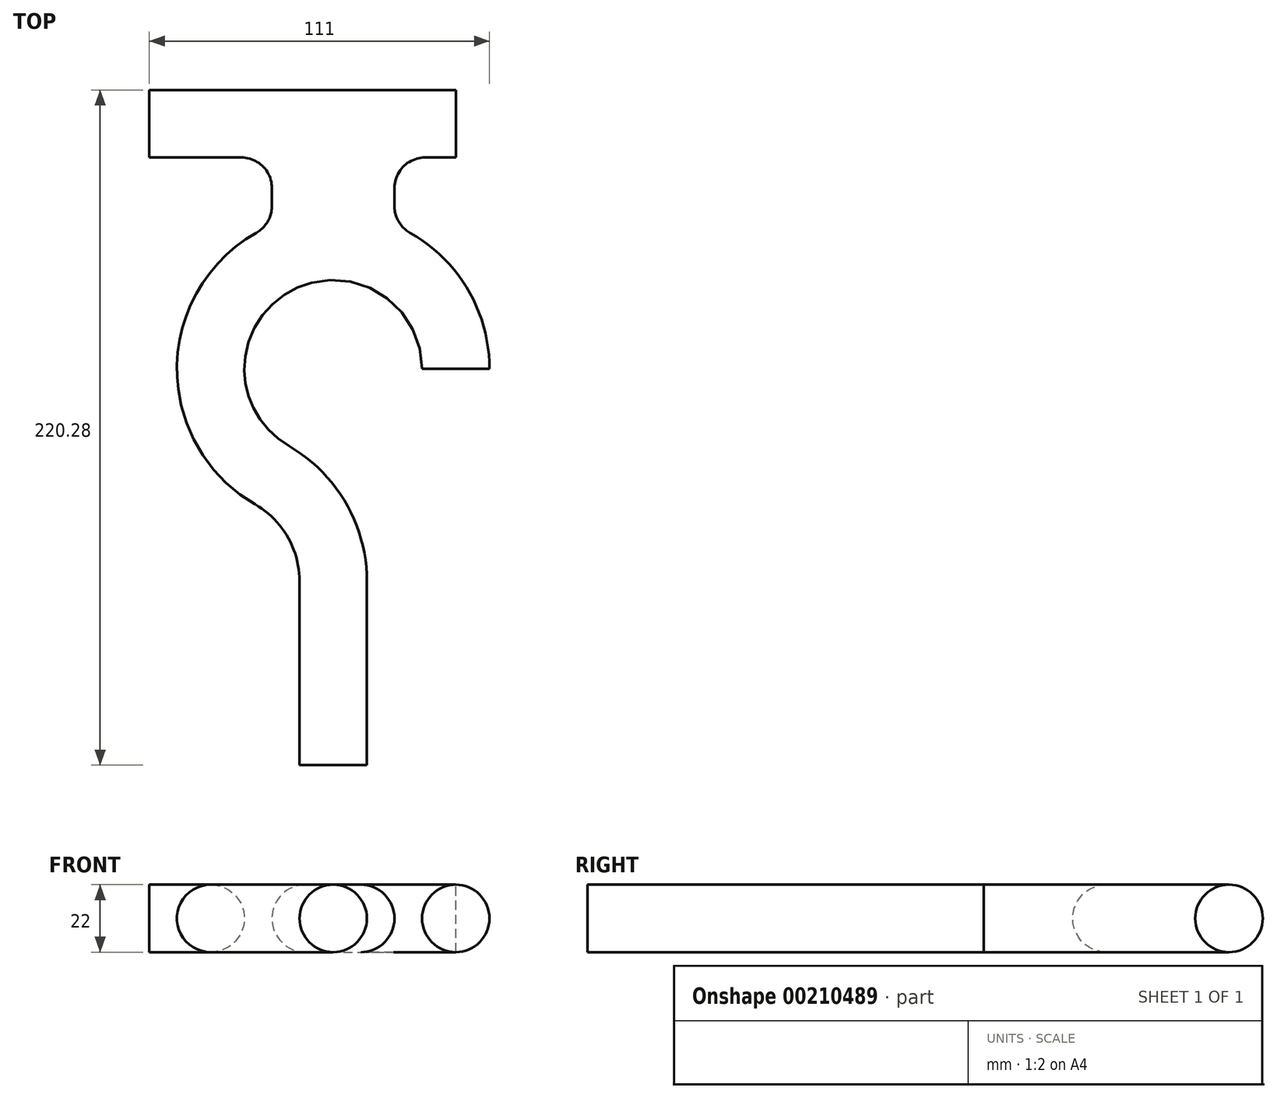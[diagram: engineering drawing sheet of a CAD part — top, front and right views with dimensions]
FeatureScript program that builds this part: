
annotation { "Feature Type Name" : "Feature", "Feature Type Description" : "" }
export const myFeature = defineFeature(function(context is Context, id is Id, definition is map)
    precondition{}
    {
        {
            assignVariable(context, id + "F0", {"name" : "Breite", "anyValue" : 22});
        }
        {
            var Q0;
            Q0=qCreatedBy(makeId("Top.planeOp"),FACE);
            var sketch = newSketch(context, id + "F1", { "sketchPlane" : qUnion([Q0])});
            skLineSegment(sketch, "E0", {"start": v(0, -69.28) * mm, "end": v(0, -129.28) * mm});
            skArc(sketch, "E1", {"start": v(40, 0) * mm, "mid": v(-20, 34.64) * mm, "end": v(-20, -34.64) * mm});
            skArc(sketch, "E2", {"start": v(0, -69.28) * mm, "mid": v(-5.36, -49.28) * mm, "end": v(-20, -34.64) * mm});
            skSolve(sketch);
        }
        {
            var Q0;
            Q0=qCreatedBy(makeId("Front.planeOp"),FACE);
            var sketch = newSketch(context, id + "F2", { "sketchPlane" : qUnion([Q0])});
            skLineSegment(sketch, "E3.rect.bottom", {"start": v(51, -11) * mm, "end": v(29, -11) * mm});
            skLineSegment(sketch, "E3.rect.top", {"start": v(51, 11) * mm, "end": v(29, 11) * mm});
            skLineSegment(sketch, "E3.rect.left", {"start": v(51, -11) * mm, "end": v(51, 11) * mm});
            skLineSegment(sketch, "E3.rect.right", {"start": v(29, -11) * mm, "end": v(29, 11) * mm});
            skPoint(sketch, "E3.rect.middle", {"position": v(40, 0) * mm});
            skSolve(sketch);
        }
        {
            var Q0;
            Q0=makeQuery(id+"F2.imprint","IMPRINT",FACE,{"disambiguationData":[TD([[makeQuery(id+"F2.imprint","IMPRINT",EDGE,{"derivedFrom":sQuery(id+"F2.wireOp",EDGE,"E3.rect.bottom")}),-1.0]])]});
            var Q1;
            Q1=sQuery(id+"F1.wireOp",EDGE,"E1");
            var Q2;
            Q2=sQuery(id+"F1.wireOp",EDGE,"E2");
            var Q3;
            Q3=sQuery(id+"F1.wireOp",EDGE,"E0");
            sweep(context, id + "F3", {"profiles" : qUnion([Q0]), "path" : qUnion([Q1, Q2, Q3])});
        }
        {
            var Q0;
            Q0=qCreatedBy(makeId("Right.planeOp"),FACE);
            var sketch = newSketch(context, id + "F4", { "sketchPlane" : qUnion([Q0])});
            skLineSegment(sketch, "E4.rect.bottom", {"start": v(69, -11) * mm, "end": v(91, -11) * mm});
            skLineSegment(sketch, "E4.rect.top", {"start": v(69, 11) * mm, "end": v(91, 11) * mm});
            skLineSegment(sketch, "E4.rect.left", {"start": v(69, -11) * mm, "end": v(69, 11) * mm});
            skLineSegment(sketch, "E4.rect.right", {"start": v(91, -11) * mm, "end": v(91, 11) * mm});
            skPoint(sketch, "E4.rect.middle", {"position": v(80, 0) * mm});
            skSolve(sketch);
        }
        {
            var Q0;
            Q0=makeQuery(id+"F4.imprint","IMPRINT",FACE,{"disambiguationData":[TD([[makeQuery(id+"F4.imprint","IMPRINT",EDGE,{"derivedFrom":sQuery(id+"F4.wireOp",EDGE,"E4.rect.bottom")}),1.0]])]});
            extrude(context, id + "F5", {"entities" : qUnion([Q0]), "operationType" : NewBodyOperationType.ADD, "depth" : 40 * mm, "hasSecondDirection" : true, "secondDirectionOppositeDirection" : true, "secondDirectionDepth" : 60 * mm});
        }
        {
            var Q0;
            Q0=qCreatedBy(makeId("Top.planeOp"),FACE);
            var sketch = newSketch(context, id + "F6", { "sketchPlane" : qUnion([Q0])});
            skLineSegment(sketch, "E5", {"start": v(-20, 53.11) * mm, "end": v(-20, 59) * mm});
            skArc(sketch, "E6", {"start": v(-20, 59) * mm, "mid": v(-22.93, 66.07) * mm, "end": v(-30, 69) * mm});
            skArc(sketch, "E7", {"start": v(-20, 53.11) * mm, "mid": v(-21.36, 48.07) * mm, "end": v(-25.08, 44.4) * mm});
            skArc(sketch, "E8.MirrorCS", {"start": v(20, 53.11) * mm, "mid": v(21.36, 48.07) * mm, "end": v(25.08, 44.4) * mm});
            skLineSegment(sketch, "E9.MirrorCS", {"start": v(20, 53.11) * mm, "end": v(20, 59) * mm});
            skArc(sketch, "E10.MirrorCS", {"start": v(20, 59) * mm, "mid": v(22.93, 66.07) * mm, "end": v(30, 69) * mm});
            skLineSegment(sketch, "E11", {"start": v(-30, 69) * mm, "end": v(30, 69) * mm});
            skArc(sketch, "E12.0", {"start": v(51, 0) * mm, "mid": v(-25.5, 44.17) * mm, "end": v(-25.5, -44.17) * mm});
            skSolve(sketch);
        }
        {
            var Q0;
            Q0=qSketchRegion(id+"F6",true);
            extrude(context, id + "F7", {"entities" : qUnion([Q0]), "operationType" : NewBodyOperationType.ADD, "depth" : (getVariable(context, 'Breite')) / 2 * mm, "hasSecondDirection" : true, "secondDirectionOppositeDirection" : true, "secondDirectionDepth" : (getVariable(context, 'Breite')) / 2 * mm});
        }
        {
            var Q0;
            Q0=makeQuery(id+"F5.opExtrude","SWEPT_EDGE",EDGE,{"disambiguationData":[OSD([sQuery(id+"F4.wireOp",EDGE,"E4.rect.bottom"),sQuery(id+"F4.wireOp",EDGE,"E4.rect.right")])]});
            var Q1;
            {var subQ0=sQuery(id+"F4.wireOp",EDGE,"E4.rect.left");var subQ1=sQuery(id+"F4.wireOp",EDGE,"E4.rect.bottom");var subQ2=sQuery(id+"F6.wireOp",EDGE,"E10.MirrorCS");Q1=makeQuery(id+"F7.boolean.opBoolean","SPLIT",EDGE,{"disambiguationData":[TD([makeQuery(id+"F7.opExtrude","SWEPT_FACE",FACE,{"disambiguationData":[OSD([subQ2])]})])],"derivedFrom":makeQuery(id+"F5.opExtrude","SWEPT_EDGE",EDGE,{"disambiguationData":[OSD([subQ1,subQ0])]})});}
            var Q2;
            {var subQ0=sQuery(id+"F4.wireOp",EDGE,"E4.rect.left");var subQ1=sQuery(id+"F4.wireOp",EDGE,"E4.rect.bottom");var subQ2=sQuery(id+"F6.wireOp",EDGE,"E6");Q2=makeQuery(id+"F7.boolean.opBoolean","SPLIT",EDGE,{"disambiguationData":[TD([makeQuery(id+"F7.opExtrude","SWEPT_FACE",FACE,{"disambiguationData":[OSD([subQ2])]})])],"derivedFrom":makeQuery(id+"F5.opExtrude","SWEPT_EDGE",EDGE,{"disambiguationData":[OSD([subQ1,subQ0])]})});}
            var Q3;
            Q3=makeQuery(id+"F3.opSweep","SWEPT_EDGE",EDGE,{"disambiguationData":[OSD([sQuery(id+"F1.wireOp",EDGE,"E1"),sQuery(id+"F2.wireOp",EDGE,"E3.rect.bottom"),sQuery(id+"F2.wireOp",EDGE,"E3.rect.right")])]});
            var Q4;
            Q4=makeQuery(id+"F5.opExtrude","SWEPT_EDGE",EDGE,{"disambiguationData":[OSD([sQuery(id+"F4.wireOp",EDGE,"E4.rect.top"),sQuery(id+"F4.wireOp",EDGE,"E4.rect.right")])]});
            var Q5;
            {var subQ0=sQuery(id+"F4.wireOp",EDGE,"E4.rect.left");var subQ1=sQuery(id+"F4.wireOp",EDGE,"E4.rect.top");var subQ2=sQuery(id+"F6.wireOp",EDGE,"E10.MirrorCS");Q5=makeQuery(id+"F7.boolean.opBoolean","SPLIT",EDGE,{"disambiguationData":[TD([makeQuery(id+"F7.opExtrude","SWEPT_FACE",FACE,{"disambiguationData":[OSD([subQ2])]})])],"derivedFrom":makeQuery(id+"F5.opExtrude","SWEPT_EDGE",EDGE,{"disambiguationData":[OSD([subQ1,subQ0])]})});}
            var Q6;
            {var subQ0=sQuery(id+"F4.wireOp",EDGE,"E4.rect.left");var subQ1=sQuery(id+"F4.wireOp",EDGE,"E4.rect.top");var subQ2=sQuery(id+"F6.wireOp",EDGE,"E6");Q6=makeQuery(id+"F7.boolean.opBoolean","SPLIT",EDGE,{"disambiguationData":[TD([makeQuery(id+"F7.opExtrude","SWEPT_FACE",FACE,{"disambiguationData":[OSD([subQ2])]})])],"derivedFrom":makeQuery(id+"F5.opExtrude","SWEPT_EDGE",EDGE,{"disambiguationData":[OSD([subQ1,subQ0])]})});}
            var Q7;
            Q7=makeQuery(id+"F3.opSweep","SWEPT_EDGE",EDGE,{"disambiguationData":[OSD([sQuery(id+"F1.wireOp",EDGE,"E1"),sQuery(id+"F2.wireOp",EDGE,"E3.rect.top"),sQuery(id+"F2.wireOp",EDGE,"E3.rect.right")])]});
            fillet(context, id + "F8", {"entities" : qUnion([Q0, Q1, Q2, Q3, Q4, Q5, Q6, Q7]), "radius" : (getVariable(context, 'Breite') / 2) * mm, "tangentPropagation" : true, "allowEdgeOverflow" : false});
        }
    });
